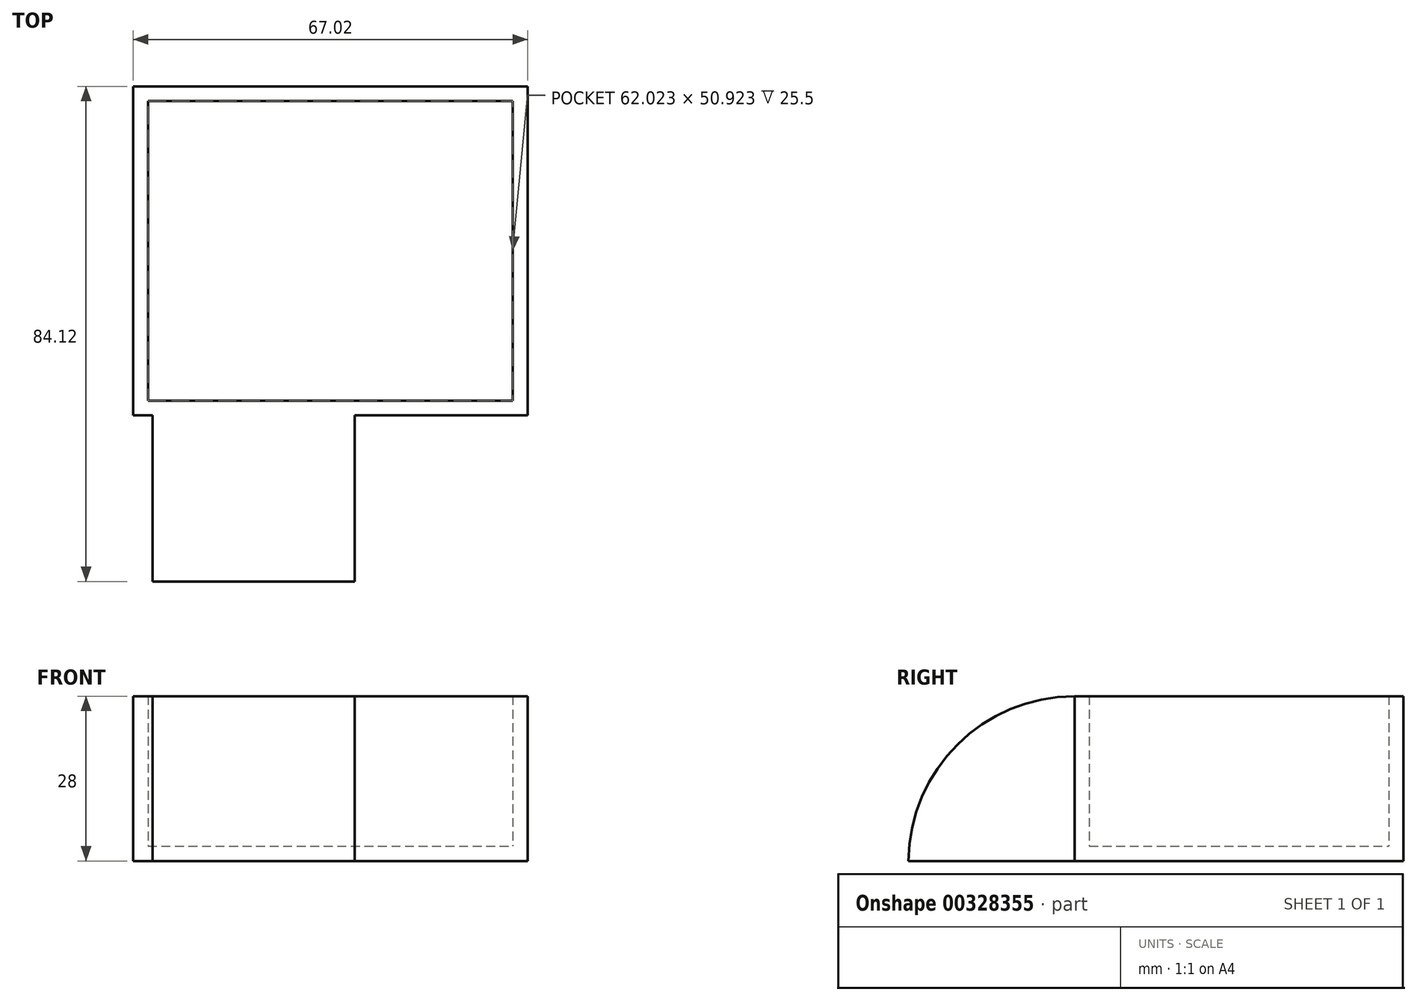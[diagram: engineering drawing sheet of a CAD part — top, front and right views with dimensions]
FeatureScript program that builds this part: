
annotation { "Feature Type Name" : "Feature", "Feature Type Description" : "" }
export const myFeature = defineFeature(function(context is Context, id is Id, definition is map)
    precondition{}
    {
        {
            var Q0;
            Q0=qCreatedBy(makeId("Top.planeOp"),FACE);
            var sketch = newSketch(context, id + "F0", { "sketchPlane" : qUnion([Q0])});
            skSolve(sketch);
        }
        {
            var Q0;
            Q0=qCreatedBy(makeId("Top.planeOp"),FACE);
            var sketch = newSketch(context, id + "F1", { "sketchPlane" : qUnion([Q0])});
            skLineSegment(sketch, "E0.bottom", {"start": v(-54.31, -38.45) * mm, "end": v(12.71, -38.45) * mm});
            skLineSegment(sketch, "E0.top", {"start": v(-54.31, 17.47) * mm, "end": v(12.71, 17.47) * mm});
            skLineSegment(sketch, "E0.left", {"start": v(-54.31, -38.45) * mm, "end": v(-54.31, 17.47) * mm});
            skLineSegment(sketch, "E0.right", {"start": v(12.71, -38.45) * mm, "end": v(12.71, 17.47) * mm});
            skSolve(sketch);
        }
        {
            var Q0;
            Q0 = qSketchRegion(id + "F0", true);
            var Q1;
            Q1 = qSketchRegion(id + "F1", true);
            extrude(context, id + "F2", {"entities" : qUnion([Q0, Q1]), "depth" : 28 * mm});
        }
        {
            var Q0;
            Q0=makeQuery(id+"F2.opExtrude","CAP_FACE",FACE,{"disambiguationData":[OSD([sQuery(id+"F1.wireOp",EDGE,"E0.bottom"),sQuery(id+"F1.wireOp",EDGE,"E0.top"),sQuery(id+"F1.wireOp",EDGE,"E0.left"),sQuery(id+"F1.wireOp",EDGE,"E0.right")])],"isStart":false});
            shell(context, id + "F3", {"entities" : qUnion([Q0]), "thickness" : 2.5 * mm});
        }
        {
            var Q0;
            Q0=makeQuery(id+"F2.opExtrude","SWEPT_FACE",FACE,{"disambiguationData":[OSD([sQuery(id+"F1.wireOp",EDGE,"E0.bottom")])]});
            var sketch = newSketch(context, id + "F4", { "sketchPlane" : qUnion([Q0])});
            skLineSegment(sketch, "E1.bottom", {"start": v(-16.69, 0) * mm, "end": v(-51, 0) * mm});
            skLineSegment(sketch, "E1.top", {"start": v(-16.69, 28) * mm, "end": v(-51, 28) * mm});
            skLineSegment(sketch, "E1.left", {"start": v(-16.69, 0) * mm, "end": v(-16.69, 28) * mm});
            skLineSegment(sketch, "E1.right", {"start": v(-51, 0) * mm, "end": v(-51, 28) * mm});
            skSolve(sketch);
        }
        {
            var Q0;
            Q0=makeQuery(id+"F4.imprint","IMPRINT",FACE,{"disambiguationData":[TD([[makeQuery(id+"F4.imprint","IMPRINT",EDGE,{"derivedFrom":sQuery(id+"F4.wireOp",EDGE,"E1.bottom")}),1.0]])]});
            extrude(context, id + "F5", {"entities" : qUnion([Q0]), "operationType" : NewBodyOperationType.ADD, "depth" : 28.2 * mm});
        }
        {
            var Q0;
            Q0=makeQuery(id+"F5.opExtrude","CAP_EDGE",EDGE,{"disambiguationData":[OSD([sQuery(id+"F4.wireOp",EDGE,"E1.top")])],"isStart":false});
            fillet(context, id + "F6", {"entities" : qUnion([Q0]), "radius" : 28.25 * mm, "tangentPropagation" : true, "allowEdgeOverflow" : false});
        }
    });
